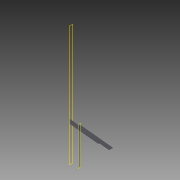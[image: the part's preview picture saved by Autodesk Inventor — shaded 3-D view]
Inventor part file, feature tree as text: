
AUTODESK INVENTOR PART (.ipt)
format: ipt  version: 2015 (Build 190159000, 159)  size: 85,504 bytes
history: native  units: in
note: dims shown in document units (in); Inventor stores cm internally (conversion verified against a paired STEP export)
features: sketch x3, plane x2, extrude x2, reference x1, projected_geometry x1
ambient origin geometry x8: Origin, YZ Plane, XZ Plane, XY Plane, X Axis, Y Axis, Z Axis, Center Point
bodies: Solid1 (feature_tree)
feature tree (9):
  plane  "Work Plane1"
  extrude  "Extrusion1"  Depth=1.5in TaperAngle=0.0deg
  plane  "Work Plane2"
  extrude  "Extrusion2"  Depth=1.5in
  sketch  "Sketch4"  dims[d6=19.5in]
  sketch  "Sketch1"  dims[d0=9.25in d1=1.5in d2=0.0in]
  reference  "Reference1"
  sketch  "Sketch2"  dims[d3=1.5in d4=0.0in d5=3.5in]
  projected_geometry  "Projected Loop1"
